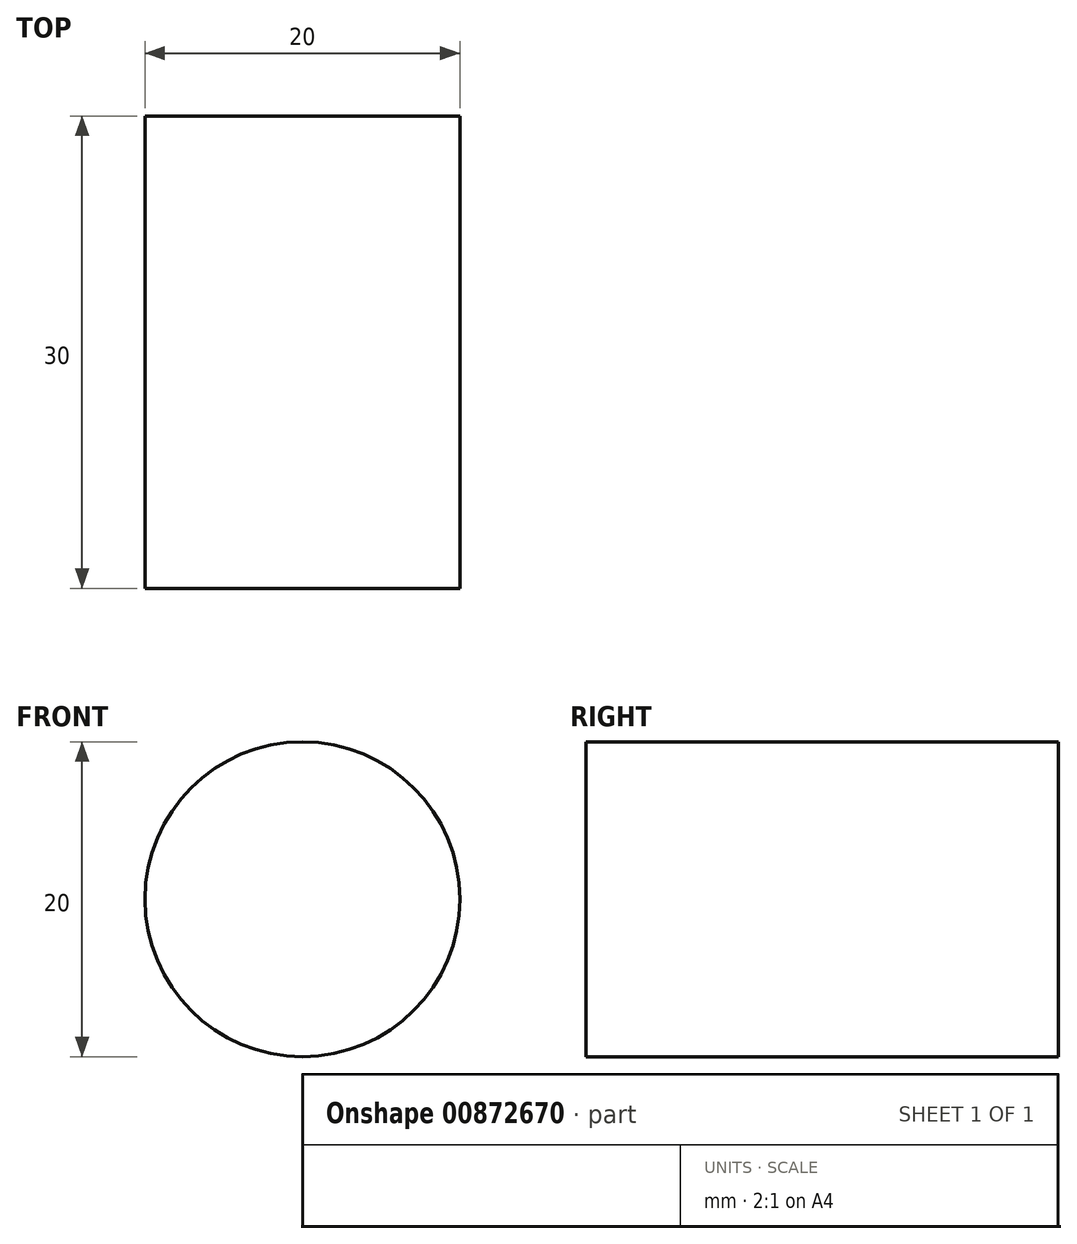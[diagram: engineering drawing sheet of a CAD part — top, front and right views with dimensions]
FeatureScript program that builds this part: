
annotation { "Feature Type Name" : "Feature", "Feature Type Description" : "" }
export const myFeature = defineFeature(function(context is Context, id is Id, definition is map)
    precondition{}
    {
        {
            var Q0;
            Q0=qCreatedBy(makeId("Front.planeOp"),FACE);
            var sketch = newSketch(context, id + "F0", { "sketchPlane" : qUnion([Q0])});
            skCircle(sketch, "E0", {"center": v(0, 0) * mm, "radius": 10 * mm});
            skSolve(sketch);
        }
        {
            var Q0;
            Q0=makeQuery(id+"F0.imprint","IMPRINT",FACE,{"disambiguationData":[TD([[makeQuery(id+"F0.imprint","IMPRINT",EDGE,{"derivedFrom":sQuery(id+"F0.wireOp",EDGE,"E0")}),1.0]])]});
            extrude(context, id + "F1", {"entities" : qUnion([Q0]), "depth" : 30 * mm, "offsetDistance" : 25 * mm});
        }
    });
